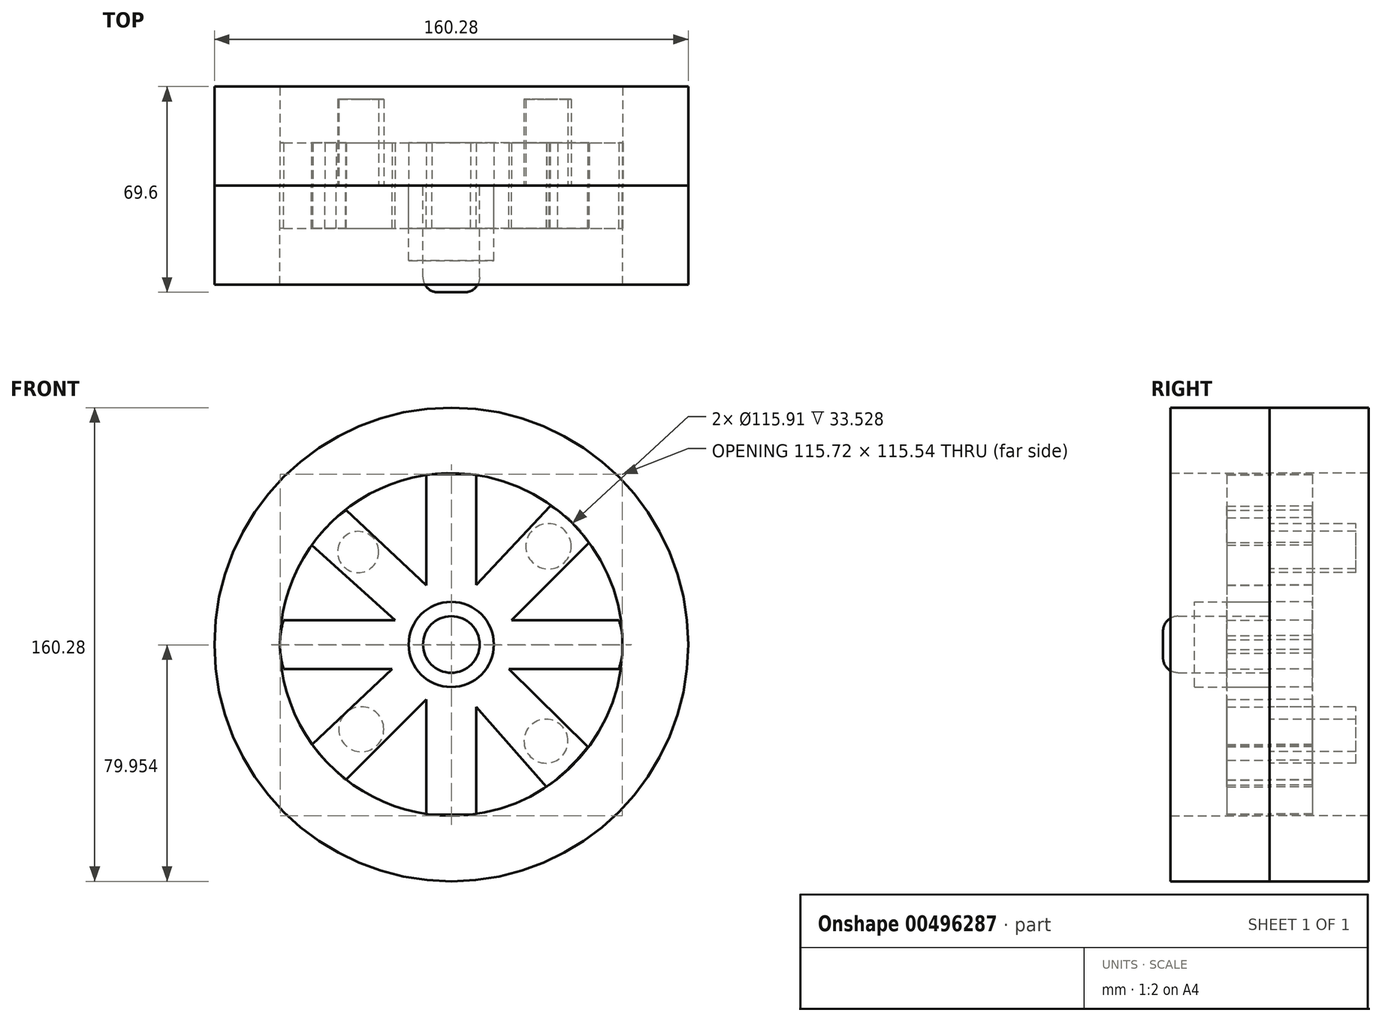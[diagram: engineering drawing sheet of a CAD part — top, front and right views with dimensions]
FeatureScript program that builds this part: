
annotation { "Feature Type Name" : "Feature", "Feature Type Description" : "" }
export const myFeature = defineFeature(function(context is Context, id is Id, definition is map)
    precondition{}
    {
        {
            var Q0;
            Q0=qCreatedBy(makeId("Front.planeOp"),FACE);
            var sketch = newSketch(context, id + "F0", { "sketchPlane" : qUnion([Q0])});
            skCircle(sketch, "E0", {"center": v(0, 0) * mm, "radius": 57.95 * mm});
            skCircle(sketch, "E1", {"center": v(0, 0) * mm, "radius": 80.14 * mm});
            skSolve(sketch);
        }
        {
            var Q0;
            Q0=qCreatedBy(makeId("Front.planeOp"),FACE);
            var sketch = newSketch(context, id + "F1", { "sketchPlane" : qUnion([Q0])});
            skCircle(sketch, "E2", {"center": v(0, 0) * mm, "radius": 14.4 * mm});
            skLineSegment(sketch, "E3.bottom", {"start": v(8.46, 57.58) * mm, "end": v(-8.46, 57.58) * mm});
            skLineSegment(sketch, "E3.top", {"start": v(8.46, -57.58) * mm, "end": v(-8.46, -57.58) * mm});
            skLineSegment(sketch, "E3.left", {"start": v(8.46, 57.58) * mm, "end": v(8.46, 20.17) * mm});
            skLineSegment(sketch, "E3.right", {"start": v(-8.46, 57.58) * mm, "end": v(-8.46, 20.06) * mm});
            skLineSegment(sketch, "E4.bottom", {"start": v(-56.7, -8.25) * mm, "end": v(-20.04, -8.25) * mm});
            skLineSegment(sketch, "E4.top", {"start": v(-56.7, 8.25) * mm, "end": v(-19.04, 8.25) * mm});
            skLineSegment(sketch, "E5", {"start": v(-47.28, 33.65) * mm, "end": v(-19.04, 8.25) * mm});
            skLineSegment(sketch, "E6", {"start": v(-35.44, 45.48) * mm, "end": v(-8.46, 20.06) * mm});
            skLineSegment(sketch, "E7", {"start": v(8.46, -21.15) * mm, "end": v(32.27, -48.19) * mm});
            skLineSegment(sketch, "E8", {"start": v(19.47, -8.25) * mm, "end": v(46.18, -34.56) * mm});
            skArc(sketch, "E9", {"start": v(-35.44, 45.48) * mm, "mid": v(-41.98, 40.18) * mm, "end": v(-47.28, 33.65) * mm});
            skLineSegment(sketch, "E10", {"start": v(-35.81, -45.9) * mm, "end": v(-8.46, -18.62) * mm});
            skLineSegment(sketch, "E11", {"start": v(-47.1, -33.78) * mm, "end": v(-20.04, -8.25) * mm});
            skLineSegment(sketch, "E12", {"start": v(46.7, 34.52) * mm, "end": v(20.35, 8.25) * mm});
            skLineSegment(sketch, "E13", {"start": v(33.52, 46.86) * mm, "end": v(8.46, 20.17) * mm});
            skArc(sketch, "E14", {"start": v(-47.1, -33.78) * mm, "mid": v(-41.8, -40.17) * mm, "end": v(-35.81, -45.9) * mm});
            skArc(sketch, "E15", {"start": v(46.7, 34.52) * mm, "mid": v(40.93, 41.57) * mm, "end": v(33.52, 46.86) * mm});
            skLineSegment(sketch, "E16.trimOffspring", {"start": v(19.47, -8.25) * mm, "end": v(56.7, -8.25) * mm});
            skLineSegment(sketch, "E17.trimOffspring", {"start": v(8.46, -21.15) * mm, "end": v(8.46, -57.58) * mm});
            skLineSegment(sketch, "E18.trimOffspring", {"start": v(20.35, 8.25) * mm, "end": v(56.7, 8.25) * mm});
            skLineSegment(sketch, "E19.trimOffspring", {"start": v(-8.46, -18.62) * mm, "end": v(-8.46, -57.58) * mm});
            skArc(sketch, "E20", {"start": v(-56.7, 8.25) * mm, "mid": v(-57.98, 0) * mm, "end": v(-56.7, -8.25) * mm});
            skArc(sketch, "E21", {"start": v(56.7, -8.25) * mm, "mid": v(58.05, 0) * mm, "end": v(56.7, 8.25) * mm});
            skArc(sketch, "E22", {"start": v(32.27, -48.19) * mm, "mid": v(39.7, -41.87) * mm, "end": v(46.18, -34.56) * mm});
            skSolve(sketch);
        }
        {
            var Q0;
            Q0 = qSketchRegion(id + "F0", true);
            extrude(context, id + "F2", {"entities" : qUnion([Q0]), "depth" : 33.53 * mm});
        }
        {
            var Q0;
            {var subQ1=sQuery(id+"F1.wireOp",EDGE,"E3.bottom");Q0=makeQuery(id+"F1.imprint","IMPRINT",FACE,{"disambiguationData":[TD([[makeQuery(id+"F1.imprint","IMPRINT",EDGE,{"derivedFrom":subQ1}),1.0]])]});}
            var Q1;
            {var subQ1=sQuery(id+"F1.wireOp",EDGE,"E3.top");Q1=makeQuery(id+"F1.imprint","IMPRINT",FACE,{"disambiguationData":[TD([[makeQuery(id+"F1.imprint","IMPRINT",EDGE,{"derivedFrom":subQ1}),-1.0]])]});}
            var Q2;
            {var subQ0=sQuery(id+"F1.wireOp",EDGE,"E4.left");Q2=makeQuery(id+"F1.imprint","IMPRINT",FACE,{"disambiguationData":[TD([[makeQuery(id+"F1.imprint","IMPRINT",EDGE,{"derivedFrom":subQ0}),-1.0]])]});}
            var Q3;
            {var subQ0=sQuery(id+"F1.wireOp",EDGE,"E4.right");Q3=makeQuery(id+"F1.imprint","IMPRINT",FACE,{"disambiguationData":[TD([[makeQuery(id+"F1.imprint","IMPRINT",EDGE,{"derivedFrom":subQ0}),1.0]])]});}
            extrude(context, id + "F3", {"entities" : qUnion([Q0, Q1, Q2, Q3]), "operationType" : NewBodyOperationType.ADD, "depth" : 14.48 * mm});
        }
        {
            var Q0;
            Q0 = qSketchRegion(id + "F1", true);
            extrude(context, id + "F4", {"entities" : qUnion([Q0]), "depth" : 14.48 * mm});
        }
        {
            var Q0;
            {var subQ0=sQuery(id+"F1.wireOp",EDGE,"E4.top");var subQ1=sQuery(id+"F1.wireOp",EDGE,"E2");var subQ2=makeQuery(id+"F1.imprint","INTERSECT",VERTEX,{"disambiguationData":[OD(1.0)],"derivedFrom":[subQ1,subQ0]});Q0=makeQuery(id+"F1.imprint","IMPRINT",FACE,{"disambiguationData":[TD([[makeQuery(id+"F1.imprint","IMPRINT",EDGE,{"disambiguationData":[TD([[subQ2,-1.0]])],"derivedFrom":subQ1}),1.0]])]});}
            extrude(context, id + "F5", {"entities" : qUnion([Q0]), "depth" : 25.4 * mm});
        }
        {
            var Q0;
            {var subQ0=sQuery(id+"F1.wireOp",EDGE,"E3.left");var subQ1=sQuery(id+"F1.wireOp",EDGE,"E2");var subQ2=makeQuery(id+"F1.imprint","INTERSECT",VERTEX,{"disambiguationData":[OD(0.0)],"derivedFrom":[subQ1,subQ0]});Q0=makeQuery(id+"F1.imprint","IMPRINT",FACE,{"disambiguationData":[TD([[makeQuery(id+"F1.imprint","IMPRINT",EDGE,{"disambiguationData":[TD([[subQ2,-1.0]])],"derivedFrom":subQ1}),1.0]])]});}
            var Q1;
            {var subQ0=sQuery(id+"F1.wireOp",EDGE,"E4.top");var subQ1=sQuery(id+"F1.wireOp",EDGE,"E2");var subQ2=makeQuery(id+"F1.imprint","INTERSECT",VERTEX,{"disambiguationData":[OD(0.0)],"derivedFrom":[subQ1,subQ0]});Q1=makeQuery(id+"F1.imprint","IMPRINT",FACE,{"disambiguationData":[TD([[makeQuery(id+"F1.imprint","IMPRINT",EDGE,{"disambiguationData":[TD([[subQ2,1.0]])],"derivedFrom":subQ1}),1.0]])]});}
            var Q2;
            {var subQ0=sQuery(id+"F1.wireOp",EDGE,"E3.right");var subQ1=sQuery(id+"F1.wireOp",EDGE,"E2");var subQ2=makeQuery(id+"F1.imprint","INTERSECT",VERTEX,{"disambiguationData":[OD(1.0)],"derivedFrom":[subQ1,subQ0]});Q2=makeQuery(id+"F1.imprint","IMPRINT",FACE,{"disambiguationData":[TD([[makeQuery(id+"F1.imprint","IMPRINT",EDGE,{"disambiguationData":[TD([[subQ2,-1.0]])],"derivedFrom":subQ1}),1.0]])]});}
            extrude(context, id + "F6", {"entities" : qUnion([Q0, Q1, Q2]), "depth" : 25.4 * mm});
        }
        {
            var Q0;
            Q0=qCreatedBy(makeId("Front.planeOp"),FACE);
            var sketch = newSketch(context, id + "F7", { "sketchPlane" : qUnion([Q0])});
            skCircle(sketch, "E23", {"center": v(0, 0) * mm, "radius": 9.57 * mm});
            skSolve(sketch);
        }
        {
            var Q0;
            Q0 = qSketchRegion(id + "F7", true);
            extrude(context, id + "F8", {"entities" : qUnion([Q0]), "depth" : 36.07 * mm});
        }
        {
            var Q0;
            Q0=makeQuery(id+"F2.opExtrude","SWEPT_BODY",BODY,{"disambiguationData":[OSD([sQuery(id+"F0.wireOp",EDGE,"E0"),sQuery(id+"F0.wireOp",EDGE,"E1")])]});
            var Q1;
            Q1=makeQuery(id+"F4.opExtrude","SWEPT_BODY",BODY,{"disambiguationData":[OSD([sQuery(id+"F1.wireOp",EDGE,"E2"),sQuery(id+"F1.wireOp",EDGE,"E3.bottom"),sQuery(id+"F1.wireOp",EDGE,"E3.top"),sQuery(id+"F1.wireOp",EDGE,"E3.left"),sQuery(id+"F1.wireOp",EDGE,"E3.right"),sQuery(id+"F1.wireOp",EDGE,"E4.bottom"),sQuery(id+"F1.wireOp",EDGE,"E4.top"),sQuery(id+"F1.wireOp",EDGE,"E4.left"),sQuery(id+"F1.wireOp",EDGE,"E4.right"),sQuery(id+"F1.wireOp",EDGE,"E5"),sQuery(id+"F1.wireOp",EDGE,"E6"),sQuery(id+"F1.wireOp",EDGE,"E7"),sQuery(id+"F1.wireOp",EDGE,"E8"),sQuery(id+"F1.wireOp",EDGE,"E9"),sQuery(id+"F1.wireOp",EDGE,"lAMzv7rI-mo61-pvRp-uNpj-XgcQ4rIMlD1L"),sQuery(id+"F1.wireOp",EDGE,"E10"),sQuery(id+"F1.wireOp",EDGE,"E11"),sQuery(id+"F1.wireOp",EDGE,"E12"),sQuery(id+"F1.wireOp",EDGE,"E13"),sQuery(id+"F1.wireOp",EDGE,"E14"),sQuery(id+"F1.wireOp",EDGE,"E15"),sQuery(id+"F1.wireOp",EDGE,"E16.trimOffspring"),sQuery(id+"F1.wireOp",EDGE,"E17.trimOffspring"),sQuery(id+"F1.wireOp",EDGE,"E18.trimOffspring"),sQuery(id+"F1.wireOp",EDGE,"E19.trimOffspring")])]});
            var Q2;
            Q2=qCreatedBy(makeId("Front.planeOp"),FACE);
            mirror(context, id + "F9", {"entities" : qUnion([Q0, Q1]), "mirrorPlane" : qUnion([Q2])});
        }
        {
            var Q0;
            Q0=makeQuery(id+"F8.opExtrude","CAP_FACE",FACE,{"disambiguationData":[OSD([sQuery(id+"F7.wireOp",EDGE,"E23")])],"isStart":false});
            fillet(context, id + "F10", {"entities" : qUnion([Q0]), "radius" : 5.08 * mm, "tangentPropagation" : true, "allowEdgeOverflow" : false});
        }
        {
            var Q0;
            Q0=qCreatedBy(makeId("Front.planeOp"),FACE);
            var sketch = newSketch(context, id + "F11", { "sketchPlane" : qUnion([Q0])});
            skCircle(sketch, "E24", {"center": v(32.89, 33.23) * mm, "radius": 7.67 * mm});
            skCircle(sketch, "E25", {"center": v(-31.5, 31.3) * mm, "radius": 6.96 * mm});
            skCircle(sketch, "E26", {"center": v(-30.43, -28.69) * mm, "radius": 7.6 * mm});
            skCircle(sketch, "E27", {"center": v(32.03, -32.71) * mm, "radius": 7.44 * mm});
            skSolve(sketch);
        }
        {
            var Q0;
            Q0 = qSketchRegion(id + "F11", true);
            extrude(context, id + "F12", {"entities" : qUnion([Q0]), "oppositeDirection" : true, "depth" : 29.2 * mm});
        }
    });
